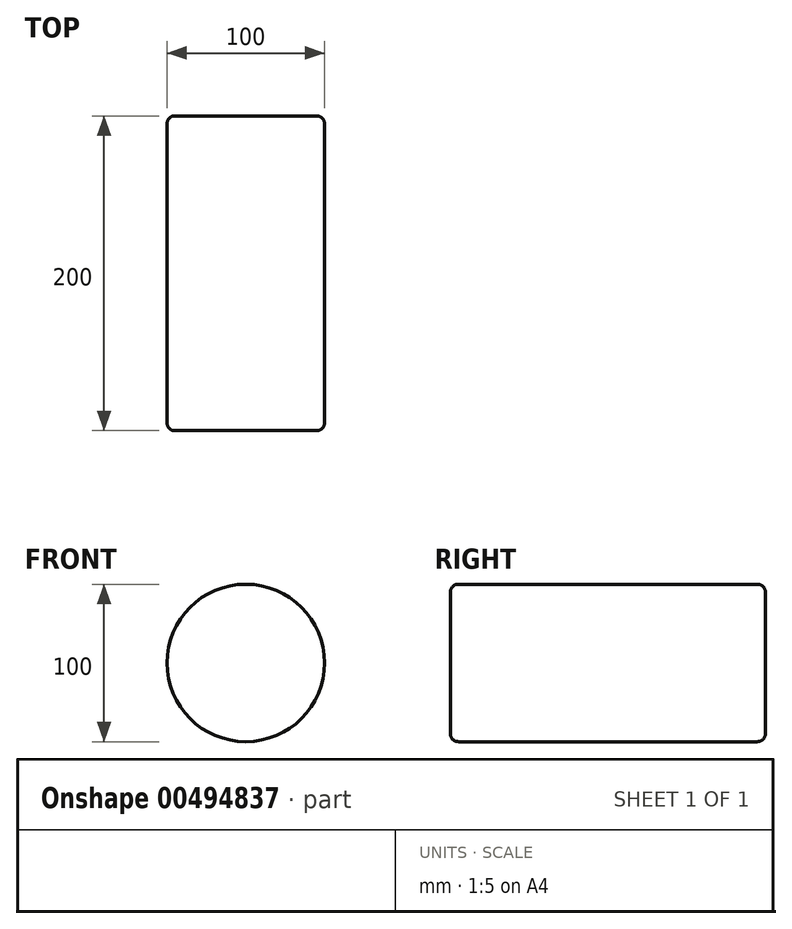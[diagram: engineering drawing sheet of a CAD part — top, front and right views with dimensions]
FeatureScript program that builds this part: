
annotation { "Feature Type Name" : "Feature", "Feature Type Description" : "" }
export const myFeature = defineFeature(function(context is Context, id is Id, definition is map)
    precondition{}
    {
        {
            var Q0;
            Q0=qCreatedBy(makeId("Front.planeOp"),FACE);
            var sketch = newSketch(context, id + "F0", { "sketchPlane" : qUnion([Q0])});
            skCircle(sketch, "E0", {"center": v(0, 0) * mm, "radius": 50 * mm});
            skSolve(sketch);
        }
        {
            var Q0;
            Q0=qSketchRegion(id+"F0",true);
            extrude(context, id + "F1", {"entities" : qUnion([Q0]), "oppositeDirection" : true, "depth" : 200 * mm});
        }
        {
            var Q0;
            Q0=makeQuery(id+"F1.opExtrude","CAP_EDGE",EDGE,{"disambiguationData":[OSD([sQuery(id+"F0.wireOp",EDGE,"E0")])],"isStart":false});
            var Q1;
            Q1=makeQuery(id+"F1.opExtrude","CAP_EDGE",EDGE,{"disambiguationData":[OSD([sQuery(id+"F0.wireOp",EDGE,"E0")])],"isStart":true});
            fillet(context, id + "F2", {"entities" : qUnion([Q0, Q1]), "radius" : 5 * mm, "tangentPropagation" : true, "allowEdgeOverflow" : false});
        }
    });
